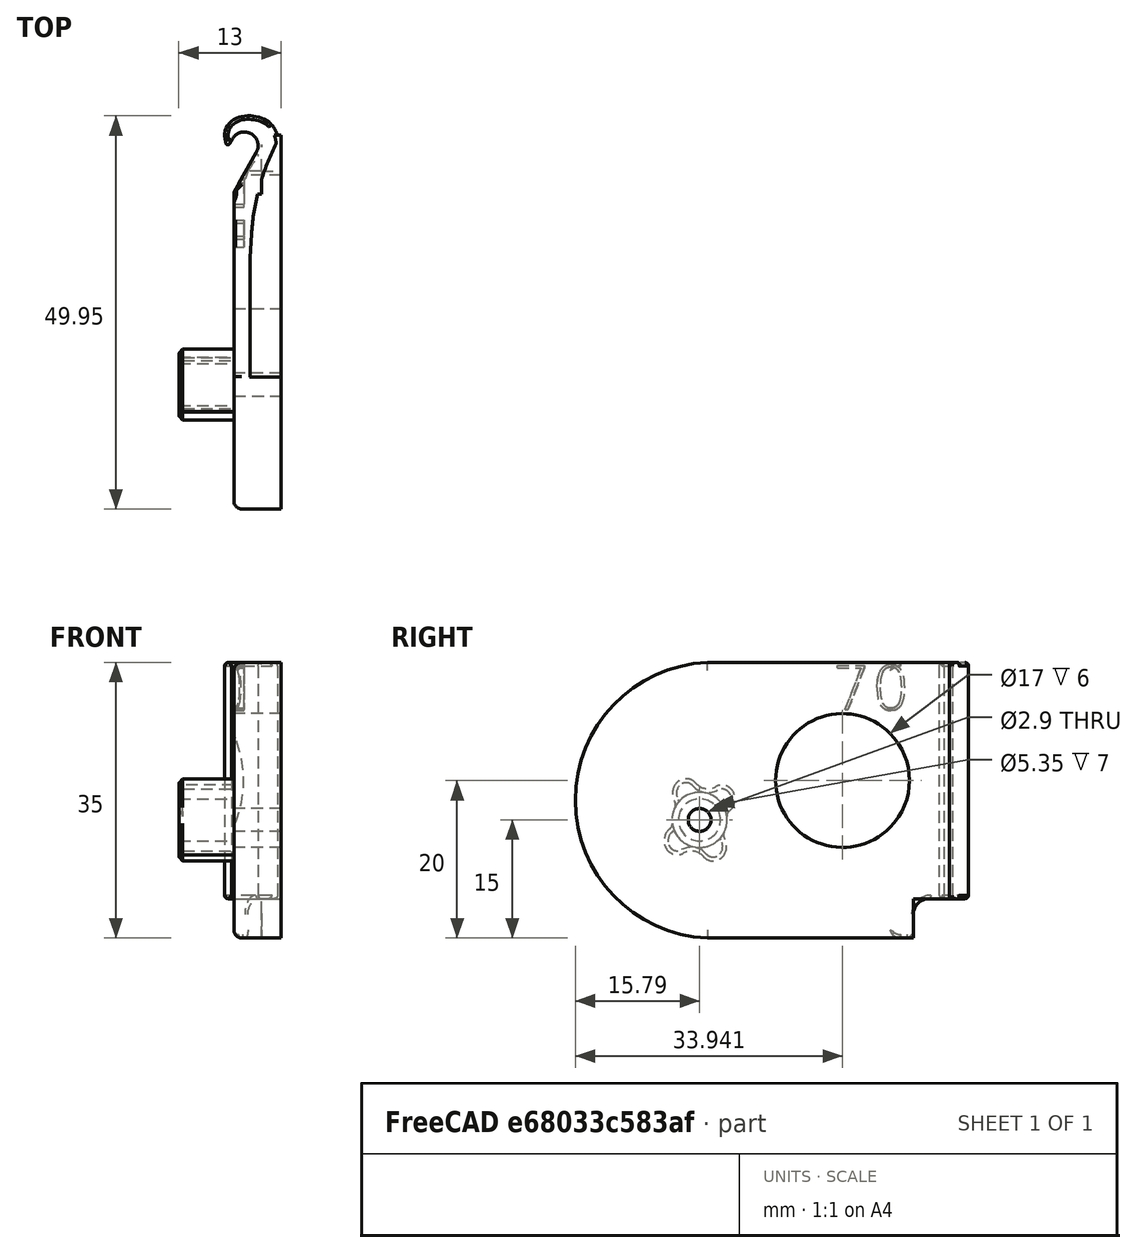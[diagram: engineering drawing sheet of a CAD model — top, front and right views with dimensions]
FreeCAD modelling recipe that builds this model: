
FCSTD DOCUMENT  (FreeCAD 0.18R)
Label: hinge-right-170deg-flat
License: All rights reserved
LicenseURL: http://en.wikipedia.org/wiki/All_rights_reserved
objects: App::FeaturePython×4, Part::FeaturePython×2, Part::Part2DObjectPython×1, Part::Extrusion×1, Part::Cut×1
note: 5 computed .brp shape members not serialized (recipe doc carries the construction recipe); baked Part::Feature solids carry a one-line shape summary decoded from their .brp

FEATURE [Part::FeaturePython] pillar_base_001  label="pillar-base_001"  # a2plus imported part (geometry in sourceFile) (typed FeaturePython)
  Placement = pos=(0.000608724,-58.3761,18.4003) rot=(-1,0,0;0.610691rad)
  a2p_Version = V0.1
  fixedPosition = false
  objectType = a2pPart
  sourceFile = ./parts/pillar-base.fcstd
  subassemblyImport = false
  timeLastImport = 1.60452e+09
  updateColors = true
FEATURE [Part::Part2DObjectPython] ShapeString  # Draft 2D object (typed FeaturePython)
  FontFile = <path>
  Placement = pos=(1.61,10.5,29) rot=(0.57735,-0.57735,-0.57735;2.0944rad)
  Size = 6
  String = 70
  Tracking = 0
FEATURE [Part::Extrusion] Extrude
  Base = -> ShapeString
  Dir = (-1,0,0)
  DirMode = 2
  FaceMakerClass = Part::FaceMakerBullseye
  LengthFwd = 3.5
  LengthRev = 0
  Placement = pos=(0,0,0) rot=(0,0,1;3.14159rad)
  Solid = false
  Symmetric = false
FEATURE [Part::FeaturePython] bracket_right_flat_001  label="bracket-right-flat_001"  # a2plus imported part (geometry in sourceFile) (typed FeaturePython)
  Placement = pos=(0,0,0) rot=(0,0,1;3.14159rad)
  a2p_Version = V0.1
  fixedPosition = true
  objectType = a2pPart
  sourceFile = ./parts/bracket-right-flat.fcstd
  subassemblyImport = false
  timeLastImport = 1.60489e+09
  updateColors = true
FEATURE [App::FeaturePython] axisCoincident_001  label="axisCoincident_001__bracket-right-flat_001"  # a2plus constraint (typed FeaturePython)
  Object1 = pillar_base_001
  Object2 = bracket_right_flat_001
  ParentTreeObject = -> pillar_base_001
  SubElement1 = Face17
  SubElement2 = Face31
  Suppressed = false
  Type = axial
  directionConstraint = 1
  lockRotation = false
FEATURE [App::FeaturePython] axisCoincident_001_mirror  label="axisCoincident_001__pillar-base_001"  # a2plus constraint (typed FeaturePython)
  Object1 = pillar_base_001
  Object2 = bracket_right_flat_001
  ParentTreeObject = -> bracket_right_flat_001
  SubElement1 = Face17
  SubElement2 = Face31
  Suppressed = false
  Type = axial
  directionConstraint = 1
  lockRotation = false
FEATURE [App::FeaturePython] planeCoincident_001  label="planeCoincident_001__bracket-right-flat_001"  # a2plus constraint (typed FeaturePython)
  Object1 = pillar_base_001
  Object2 = bracket_right_flat_001
  ParentTreeObject = -> pillar_base_001
  SubElement1 = Face1
  SubElement2 = Face57
  Suppressed = false
  Type = plane
  directionConstraint = 1
  offset = 0
FEATURE [App::FeaturePython] planeCoincident_001_mirror  label="planeCoincident_001__pillar-base_001"  # a2plus constraint (typed FeaturePython)
  Object1 = pillar_base_001
  Object2 = bracket_right_flat_001
  ParentTreeObject = -> bracket_right_flat_001
  SubElement1 = Face1
  SubElement2 = Face57
  Suppressed = false
  Type = plane
  directionConstraint = 1
  offset = 0
FEATURE [Part::Cut] Cut
  Base = -> bracket_right_flat_001
  Tool = -> Extrude
note: 1 file-system path scrubbed to <path> (originals preserved in the JSON sidecar)
